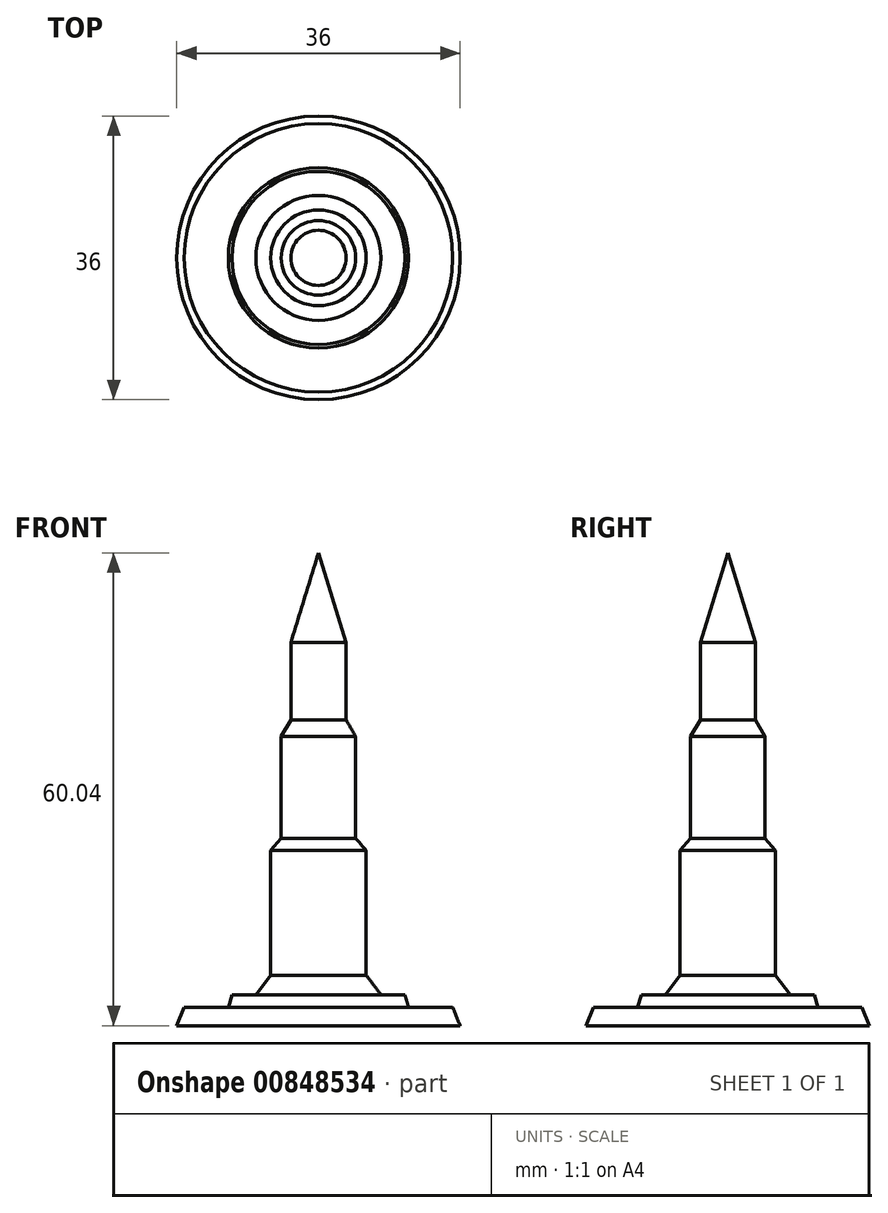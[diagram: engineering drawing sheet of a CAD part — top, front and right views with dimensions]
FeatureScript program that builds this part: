
annotation { "Feature Type Name" : "Feature", "Feature Type Description" : "" }
export const myFeature = defineFeature(function(context is Context, id is Id, definition is map)
    precondition{}
    {
        {
            var Q0;
            Q0=qCreatedBy(makeId("Front.planeOp"),FACE);
            var sketch = newSketch(context, id + "F0", { "sketchPlane" : qUnion([Q0])});
            skLineSegment(sketch, "E0", {"start": v(0, -19.53) * mm, "end": v(18, -19.53) * mm});
            skLineSegment(sketch, "E1", {"start": v(18, -19.53) * mm, "end": v(17.05, -17.2) * mm});
            skLineSegment(sketch, "E2", {"start": v(11.45, -17.2) * mm, "end": v(17.05, -17.2) * mm});
            skLineSegment(sketch, "E3", {"start": v(11.45, -17.2) * mm, "end": v(10.98, -15.6) * mm});
            skLineSegment(sketch, "E4", {"start": v(10.98, -15.6) * mm, "end": v(7.94, -15.6) * mm});
            skLineSegment(sketch, "E5", {"start": v(7.94, -15.6) * mm, "end": v(6.07, -13.11) * mm});
            skLineSegment(sketch, "E6", {"start": v(6.07, -13.11) * mm, "end": v(6.07, 2.72) * mm});
            skLineSegment(sketch, "E7", {"start": v(6.07, 2.72) * mm, "end": v(4.73, 4.28) * mm});
            skLineSegment(sketch, "E8", {"start": v(4.73, 4.28) * mm, "end": v(4.73, 17.21) * mm});
            skLineSegment(sketch, "E9", {"start": v(4.73, 17.21) * mm, "end": v(3.5, 19.33) * mm});
            skLineSegment(sketch, "E10", {"start": v(3.5, 19.33) * mm, "end": v(3.5, 29.14) * mm});
            skLineSegment(sketch, "E11", {"start": v(3.5, 29.14) * mm, "end": v(0, 40.51) * mm});
            skLineSegment(sketch, "E12", {"start": v(0, 40.51) * mm, "end": v(0, -19.53) * mm});
            skSolve(sketch);
        }
        {
            var Q0;
            Q0 = qSketchRegion(id + "F0", true);
            var Q1;
            Q1=sQuery(id+"F0.wireOp",EDGE,"E12");
            revolve(context, id + "F1", {"surfaceOperationType" : NewSurfaceOperationType.NEW, "entities" : qUnion([Q0]), "axis" : qUnion([Q1]), "revolveType" : RevolveType.FULL});
        }
    });
